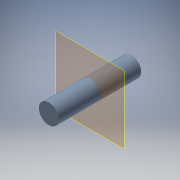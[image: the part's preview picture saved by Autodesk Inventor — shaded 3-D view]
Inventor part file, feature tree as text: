
AUTODESK INVENTOR PART (.ipt)
format: ipt  version: 2019 (Build 230136000, 136)  size: 96,768 bytes
history: native  units: mm
features: other x4, extrude x1, sketch x1, reference x1
ambient origin geometry x8: Origin, YZ Plane, XZ Plane, XY Plane, X Axis, Y Axis, Z Axis, Center Point
bodies: Body1 (feature_tree)
feature tree (7):
  other  "作業平面1"
  extrude  "押し出し2"  Depth=0.2mm
  sketch  "スケッチ2"
  reference  "参照2"
  other  "<userpath>\OneDrive\デスクトップ\mini_robot\mini_robot.iam"
  other  "mini_robot.iam"
  other  "head:1"
